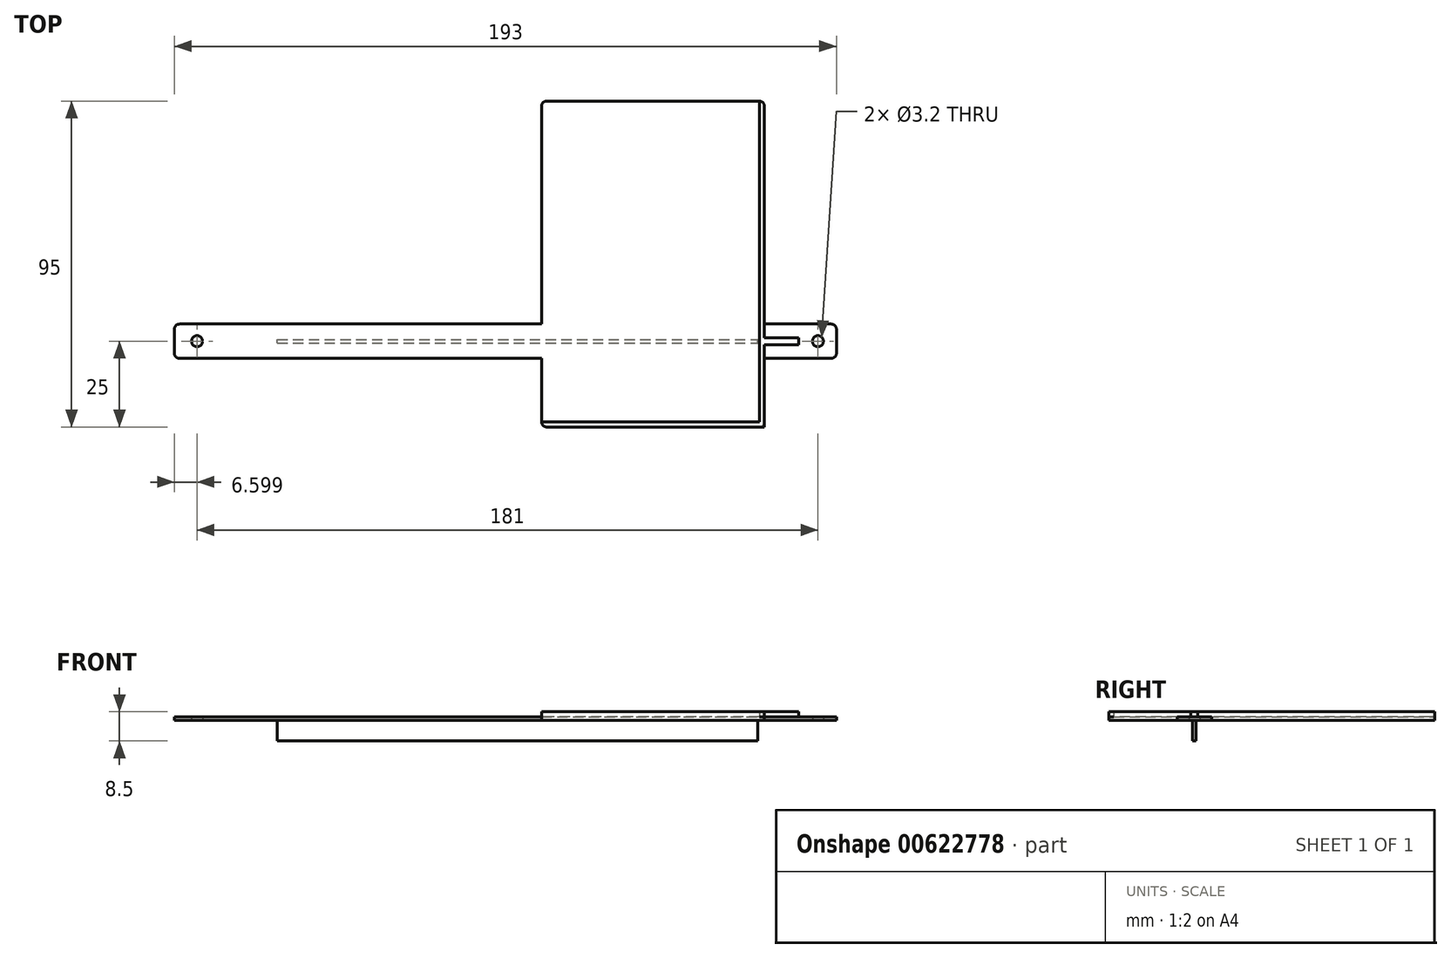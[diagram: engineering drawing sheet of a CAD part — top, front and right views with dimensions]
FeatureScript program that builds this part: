
annotation { "Feature Type Name" : "Feature", "Feature Type Description" : "" }
export const myFeature = defineFeature(function(context is Context, id is Id, definition is map)
    precondition{}
    {
        {
            var Q0;
            Q0=qCreatedBy(makeId("Top.planeOp"),FACE);
            var sketch = newSketch(context, id + "F0", { "sketchPlane" : qUnion([Q0])});
            skLineSegment(sketch, "E0", {"start": v(-37.58, 0) * mm, "end": v(-37.58, -10) * mm});
            skLineSegment(sketch, "E1", {"start": v(-37.58, -10) * mm, "end": v(69.42, -10) * mm});
            skLineSegment(sketch, "E2", {"start": v(69.42, -10) * mm, "end": v(69.42, -30) * mm});
            skLineSegment(sketch, "E3", {"start": v(69.42, -30) * mm, "end": v(134.42, -30) * mm});
            skLineSegment(sketch, "E4", {"start": v(134.42, -30) * mm, "end": v(134.42, -10) * mm});
            skLineSegment(sketch, "E5", {"start": v(134.42, -10) * mm, "end": v(155.42, -10) * mm});
            skLineSegment(sketch, "E6", {"start": v(155.42, -10) * mm, "end": v(155.42, 0) * mm});
            skLineSegment(sketch, "E7", {"start": v(155.42, 0) * mm, "end": v(134.42, 0) * mm});
            skLineSegment(sketch, "E8", {"start": v(134.42, 0) * mm, "end": v(134.42, 65) * mm});
            skLineSegment(sketch, "E9", {"start": v(134.42, 65) * mm, "end": v(69.42, 65) * mm});
            skLineSegment(sketch, "E10", {"start": v(69.42, 65) * mm, "end": v(69.42, 0) * mm});
            skLineSegment(sketch, "E11", {"start": v(69.42, 0) * mm, "end": v(-37.58, 0) * mm});
            skCircle(sketch, "E12", {"center": v(-30.98, -5) * mm, "radius": 1.6 * mm});
            skCircle(sketch, "E13", {"center": v(150.02, -5) * mm, "radius": 1.6 * mm});
            skSolve(sketch);
        }
        {
            var Q0;
            Q0=makeQuery(id+"F0.imprint","IMPRINT",FACE,{"disambiguationData":[TD([[makeQuery(id+"F0.imprint","IMPRINT",EDGE,{"derivedFrom":sQuery(id+"F0.wireOp",EDGE,"E0")}),1.0]])]});
            extrude(context, id + "F1", {"entities" : qUnion([Q0]), "depth" : 1 * mm, "offsetDistance" : 25 * mm});
        }
        {
            var Q0;
            Q0=makeQuery(id+"F1.opExtrude","SWEPT_EDGE",EDGE,{"disambiguationData":[OSD([sQuery(id+"F0.wireOp",EDGE,"E0"),sQuery(id+"F0.wireOp",EDGE,"E11")])]});
            var Q1;
            Q1=makeQuery(id+"F1.opExtrude","SWEPT_EDGE",EDGE,{"disambiguationData":[OSD([sQuery(id+"F0.wireOp",EDGE,"E0"),sQuery(id+"F0.wireOp",EDGE,"E1")])]});
            var Q2;
            Q2=makeQuery(id+"F1.opExtrude","SWEPT_EDGE",EDGE,{"disambiguationData":[OSD([sQuery(id+"F0.wireOp",EDGE,"E6"),sQuery(id+"F0.wireOp",EDGE,"E7")])]});
            var Q3;
            Q3=makeQuery(id+"F1.opExtrude","SWEPT_EDGE",EDGE,{"disambiguationData":[OSD([sQuery(id+"F0.wireOp",EDGE,"E5"),sQuery(id+"F0.wireOp",EDGE,"E6")])]});
            var Q4;
            Q4=makeQuery(id+"F1.opExtrude","SWEPT_EDGE",EDGE,{"disambiguationData":[OSD([sQuery(id+"F0.wireOp",EDGE,"E3"),sQuery(id+"F0.wireOp",EDGE,"E4")])]});
            var Q5;
            Q5=makeQuery(id+"F1.opExtrude","SWEPT_EDGE",EDGE,{"disambiguationData":[OSD([sQuery(id+"F0.wireOp",EDGE,"E2"),sQuery(id+"F0.wireOp",EDGE,"E3")])]});
            var Q6;
            Q6=makeQuery(id+"F1.opExtrude","SWEPT_EDGE",EDGE,{"disambiguationData":[OSD([sQuery(id+"F0.wireOp",EDGE,"E9"),sQuery(id+"F0.wireOp",EDGE,"E10")])]});
            var Q7;
            Q7=makeQuery(id+"F1.opExtrude","SWEPT_EDGE",EDGE,{"disambiguationData":[OSD([sQuery(id+"F0.wireOp",EDGE,"E8"),sQuery(id+"F0.wireOp",EDGE,"E9")])]});
            fillet(context, id + "F2", {"entities" : qUnion([Q0, Q1, Q2, Q3, Q4, Q5, Q6, Q7]), "radius" : 1.5 * mm, "tangentPropagation" : true, "allowEdgeOverflow" : false});
        }
        {
            var Q0;
            Q0=makeQuery(id+"F1.opExtrude","CAP_FACE",FACE,{"disambiguationData":[OSD([sQuery(id+"F0.wireOp",EDGE,"E0"),sQuery(id+"F0.wireOp",EDGE,"E1"),sQuery(id+"F0.wireOp",EDGE,"E2"),sQuery(id+"F0.wireOp",EDGE,"E3"),sQuery(id+"F0.wireOp",EDGE,"E4"),sQuery(id+"F0.wireOp",EDGE,"E5"),sQuery(id+"F0.wireOp",EDGE,"E6"),sQuery(id+"F0.wireOp",EDGE,"E7"),sQuery(id+"F0.wireOp",EDGE,"E8"),sQuery(id+"F0.wireOp",EDGE,"E9"),sQuery(id+"F0.wireOp",EDGE,"E10"),sQuery(id+"F0.wireOp",EDGE,"E11"),sQuery(id+"F0.wireOp",EDGE,"E12"),sQuery(id+"F0.wireOp",EDGE,"E13")])],"isStart":true});
            var sketch = newSketch(context, id + "F3", { "sketchPlane" : qUnion([Q0])});
            skLineSegment(sketch, "E14.bottom", {"start": v(-7.58, 5.5) * mm, "end": v(132.42, 5.5) * mm});
            skLineSegment(sketch, "E14.top", {"start": v(-7.58, 4.5) * mm, "end": v(132.42, 4.5) * mm});
            skLineSegment(sketch, "E14.left", {"start": v(-7.58, 5.5) * mm, "end": v(-7.58, 4.5) * mm});
            skLineSegment(sketch, "E14.right", {"start": v(132.42, 5.5) * mm, "end": v(132.42, 4.5) * mm});
            skSolve(sketch);
        }
        {
            var Q0;
            Q0=makeQuery(id+"F3.imprint","IMPRINT",FACE,{"disambiguationData":[TD([[makeQuery(id+"F3.imprint","IMPRINT",EDGE,{"derivedFrom":sQuery(id+"F3.wireOp",EDGE,"E14.bottom")}),-1.0]])]});
            extrude(context, id + "F4", {"entities" : qUnion([Q0]), "operationType" : NewBodyOperationType.ADD, "depth" : 6 * mm, "offsetDistance" : 25 * mm});
        }
        {
            var Q0;
            Q0=makeQuery(id+"F1.opExtrude","CAP_FACE",FACE,{"disambiguationData":[OSD([sQuery(id+"F0.wireOp",EDGE,"E0"),sQuery(id+"F0.wireOp",EDGE,"E1"),sQuery(id+"F0.wireOp",EDGE,"E2"),sQuery(id+"F0.wireOp",EDGE,"E3"),sQuery(id+"F0.wireOp",EDGE,"E4"),sQuery(id+"F0.wireOp",EDGE,"E5"),sQuery(id+"F0.wireOp",EDGE,"E6"),sQuery(id+"F0.wireOp",EDGE,"E7"),sQuery(id+"F0.wireOp",EDGE,"E8"),sQuery(id+"F0.wireOp",EDGE,"E9"),sQuery(id+"F0.wireOp",EDGE,"E10"),sQuery(id+"F0.wireOp",EDGE,"E11"),sQuery(id+"F0.wireOp",EDGE,"E12"),sQuery(id+"F0.wireOp",EDGE,"E13")])],"isStart":false});
            var sketch = newSketch(context, id + "F5", { "sketchPlane" : qUnion([Q0])});
            skLineSegment(sketch, "E15.bottom", {"start": v(69.42, -28.5) * mm, "end": v(134.42, -28.5) * mm});
            skLineSegment(sketch, "E15.top", {"start": v(69.42, -30) * mm, "end": v(134.42, -30) * mm});
            skLineSegment(sketch, "E15.left", {"start": v(69.42, -28.5) * mm, "end": v(69.42, -30) * mm});
            skLineSegment(sketch, "E15.right", {"start": v(134.42, -28.5) * mm, "end": v(134.42, -30) * mm});
            skLineSegment(sketch, "E16.bottom", {"start": v(134.42, -30) * mm, "end": v(132.92, -30) * mm});
            skLineSegment(sketch, "E16.top", {"start": v(134.42, 65) * mm, "end": v(132.92, 65) * mm});
            skLineSegment(sketch, "E16.left", {"start": v(134.42, -30) * mm, "end": v(134.42, 65) * mm});
            skLineSegment(sketch, "E16.right", {"start": v(132.92, -30) * mm, "end": v(132.92, 65) * mm});
            skSolve(sketch);
        }
        {
            var Q0;
            Q0 = qSketchRegion(id + "F5", true);
            extrude(context, id + "F6", {"entities" : qUnion([Q0]), "operationType" : NewBodyOperationType.ADD, "depth" : 1.5 * mm, "offsetDistance" : 25 * mm});
        }
        {
            var Q0;
            Q0=makeQuery(id+"F6.opExtrude","SWEPT_EDGE",EDGE,{"disambiguationData":[OSD([sQuery(id+"F5.wireOp",EDGE,"E16.bottom"),sQuery(id+"F5.wireOp",EDGE,"E16.left")])]});
            var Q1;
            Q1=makeQuery(id+"F6.opExtrude","SWEPT_EDGE",EDGE,{"disambiguationData":[OSD([sQuery(id+"F5.wireOp",EDGE,"E15.top"),sQuery(id+"F5.wireOp",EDGE,"E15.left")])]});
            var Q2;
            Q2=makeQuery(id+"F6.opExtrude","SWEPT_EDGE",EDGE,{"disambiguationData":[OSD([sQuery(id+"F5.wireOp",EDGE,"E16.top"),sQuery(id+"F5.wireOp",EDGE,"E16.left")])]});
            fillet(context, id + "F7", {"entities" : qUnion([Q0, Q1, Q2]), "radius" : 1.5 * mm, "tangentPropagation" : true, "allowEdgeOverflow" : false});
        }
        {
            var Q0;
            {var subQ0=sQuery(id+"F0.wireOp",EDGE,"E7");var subQ1=sQuery(id+"F0.wireOp",EDGE,"E6");var subQ2=sQuery(id+"F0.wireOp",EDGE,"E5");var subQ3=sQuery(id+"F0.wireOp",EDGE,"E4");var subQ4=sQuery(id+"F0.wireOp",EDGE,"E8");var subQ5=sQuery(id+"F0.wireOp",EDGE,"E13");Q0=makeQuery(id+"F6.boolean.opBoolean","SPLIT",FACE,{"disambiguationData":[TD([makeQuery(id+"F1.opExtrude","SWEPT_FACE",FACE,{"disambiguationData":[OSD([subQ3])]})])],"derivedFrom":makeQuery(id+"F1.opExtrude","CAP_FACE",FACE,{"disambiguationData":[OSD([sQuery(id+"F0.wireOp",EDGE,"E0"),sQuery(id+"F0.wireOp",EDGE,"E1"),sQuery(id+"F0.wireOp",EDGE,"E2"),sQuery(id+"F0.wireOp",EDGE,"E3"),subQ3,subQ2,subQ1,subQ0,subQ4,sQuery(id+"F0.wireOp",EDGE,"E9"),sQuery(id+"F0.wireOp",EDGE,"E10"),sQuery(id+"F0.wireOp",EDGE,"E11"),sQuery(id+"F0.wireOp",EDGE,"E12"),subQ5])],"isStart":false})});}
            var sketch = newSketch(context, id + "F8", { "sketchPlane" : qUnion([Q0])});
            skLineSegment(sketch, "E17.bottom", {"start": v(134.42, -4) * mm, "end": v(144.42, -4) * mm});
            skLineSegment(sketch, "E17.top", {"start": v(134.42, -6) * mm, "end": v(144.42, -6) * mm});
            skLineSegment(sketch, "E17.left", {"start": v(134.42, -4) * mm, "end": v(134.42, -6) * mm});
            skLineSegment(sketch, "E17.right", {"start": v(144.42, -4) * mm, "end": v(144.42, -6) * mm});
            skSolve(sketch);
        }
        {
            var Q0;
            Q0=makeQuery(id+"F8.imprint","IMPRINT",FACE,{"disambiguationData":[TD([[makeQuery(id+"F8.imprint","IMPRINT",EDGE,{"derivedFrom":sQuery(id+"F8.wireOp",EDGE,"E17.bottom")}),-1.0]])]});
            var Q1;
            Q1=makeQuery(id+"F6.opExtrude","CAP_FACE",FACE,{"disambiguationData":[OSD([sQuery(id+"F5.wireOp",EDGE,"E15.bottom"),sQuery(id+"F5.wireOp",EDGE,"E15.top"),sQuery(id+"F5.wireOp",EDGE,"E15.left"),sQuery(id+"F5.wireOp",EDGE,"E16.bottom"),sQuery(id+"F5.wireOp",EDGE,"E16.top"),sQuery(id+"F5.wireOp",EDGE,"E16.left"),sQuery(id+"F5.wireOp",EDGE,"E16.right")])],"isStart":false});
            extrude(context, id + "F9", {"entities" : qUnion([Q0]), "operationType" : NewBodyOperationType.ADD, "endBound" : BoundingType.UP_TO_SURFACE, "depth" : 25 * mm, "endBoundEntityFace" : qUnion([Q1]), "offsetDistance" : 25 * mm});
        }
    });
